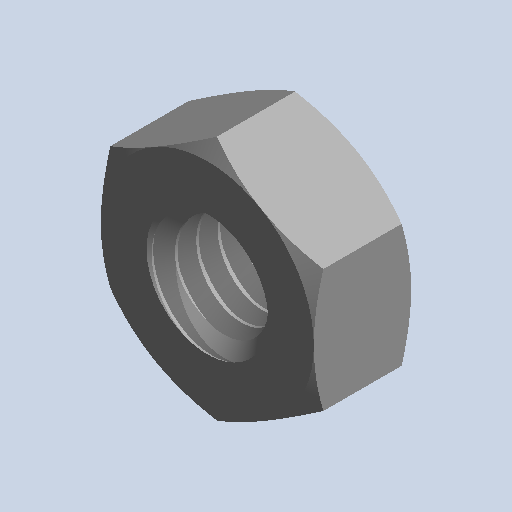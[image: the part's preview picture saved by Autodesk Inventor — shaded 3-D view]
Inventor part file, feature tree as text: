
AUTODESK INVENTOR PART (.ipt)
format: ipt  version: 2022.1 (Build 261234000, 234)  size: 220,672 bytes
history: native  units: mm (DEFAULTED — no unit token found)
features: other x8, mirror x1
bodies: Body1 (feature_tree)
feature tree (9):
  other  "Sólido1"
  other  "Origen"
  other  "Plano YZ"
  other  "Plano XZ"
  other  "Plano XY"
  other  "Eje X"
  other  "Eje Y"
  other  "Eje Z"
  mirror  "Mirror2"
